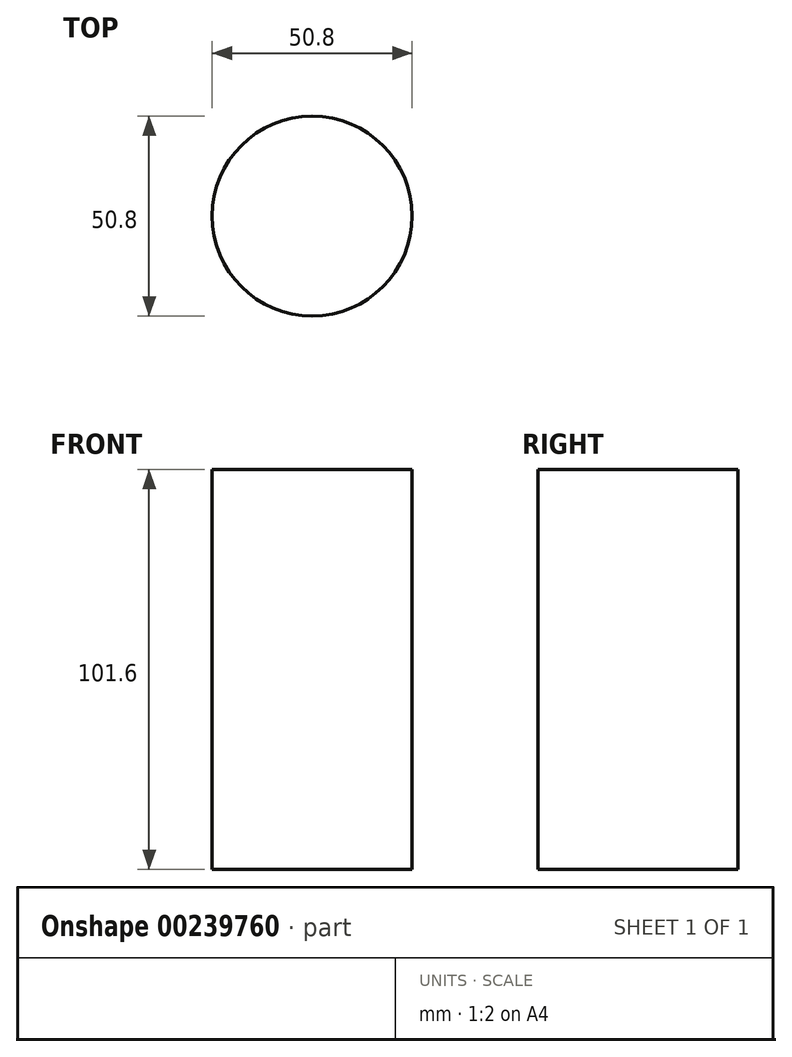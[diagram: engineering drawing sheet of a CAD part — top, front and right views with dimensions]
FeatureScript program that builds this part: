
annotation { "Feature Type Name" : "Feature", "Feature Type Description" : "" }
export const myFeature = defineFeature(function(context is Context, id is Id, definition is map)
    precondition{}
    {
        {
            var Q0;
            Q0=qCreatedBy(makeId("Top.planeOp"),FACE);
            var sketch = newSketch(context, id + "F0", { "sketchPlane" : qUnion([Q0])});
            skCircle(sketch, "E0", {"center": v(0, 0) * mm, "radius": 25.4 * mm});
            skSolve(sketch);
        }
        {
            var Q0;
            Q0 = qSketchRegion(id + "F0", true);
            extrude(context, id + "F1", {"entities" : qUnion([Q0]), "depth" : 101.6 * mm});
        }
    });
